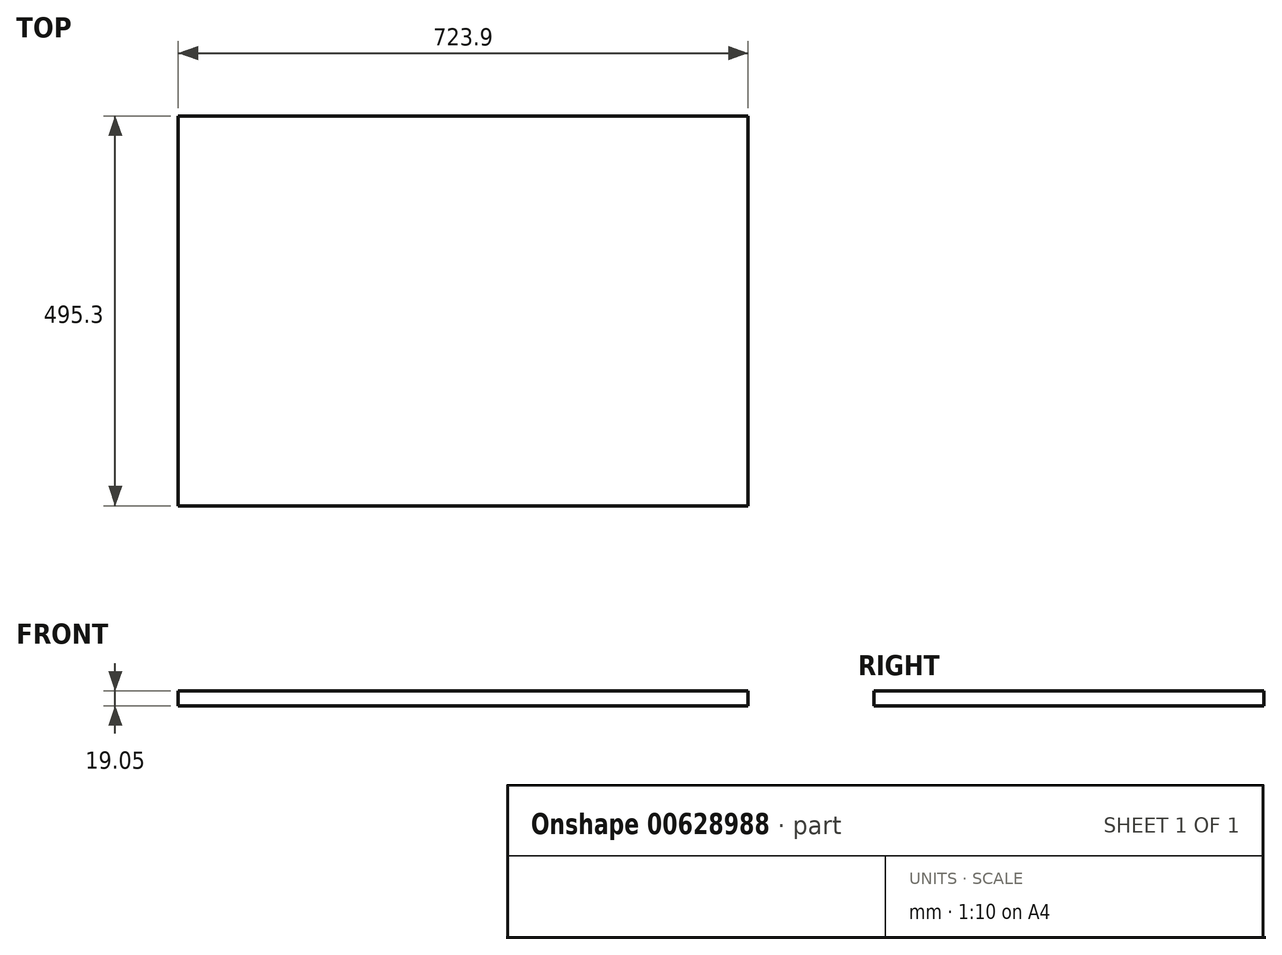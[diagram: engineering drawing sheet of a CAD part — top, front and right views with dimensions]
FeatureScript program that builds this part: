
annotation { "Feature Type Name" : "Feature", "Feature Type Description" : "" }
export const myFeature = defineFeature(function(context is Context, id is Id, definition is map)
    precondition{}
    {
        {
            var Q0;
            Q0=qCreatedBy(makeId("Top.planeOp"),FACE);
            var sketch = newSketch(context, id + "F0", { "sketchPlane" : qUnion([Q0])});
            skLineSegment(sketch, "E0.bottom", {"start": v(-361.95, 247.65) * mm, "end": v(361.95, 247.65) * mm});
            skLineSegment(sketch, "E0.top", {"start": v(-361.95, -247.65) * mm, "end": v(361.95, -247.65) * mm});
            skLineSegment(sketch, "E0.left", {"start": v(-361.95, 247.65) * mm, "end": v(-361.95, -247.65) * mm});
            skLineSegment(sketch, "E0.right", {"start": v(361.95, 247.65) * mm, "end": v(361.95, -247.65) * mm});
            skPoint(sketch, "E0.middle", {"position": v(0, 0) * mm});
            skSolve(sketch);
        }
        {
            var Q0;
            Q0=makeQuery(id+"F0.imprint","IMPRINT",FACE,{"disambiguationData":[TD([[makeQuery(id+"F0.imprint","IMPRINT",EDGE,{"derivedFrom":sQuery(id+"F0.wireOp",EDGE,"E0.bottom")}),-1.0]])]});
            extrude(context, id + "F1", {"entities" : qUnion([Q0]), "depth" : 19.05 * mm, "offsetDistance" : 25.4 * mm});
        }
    });
